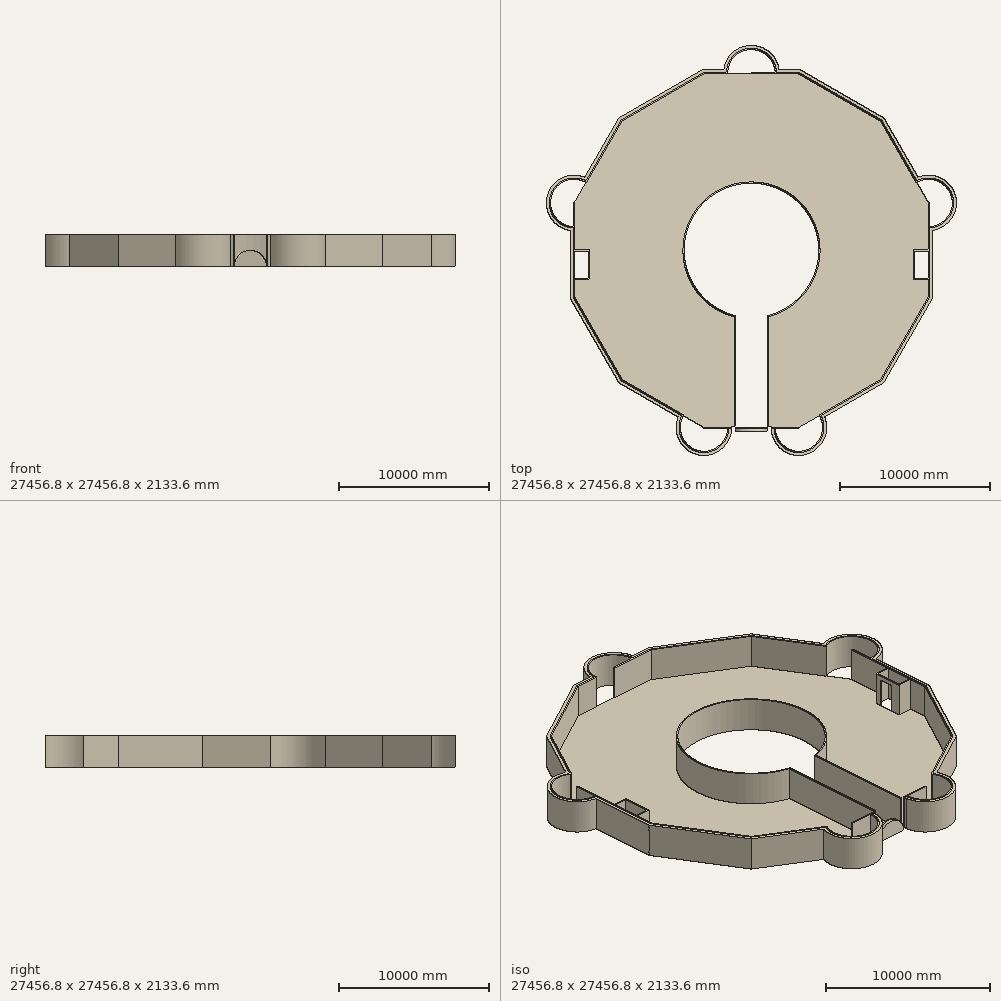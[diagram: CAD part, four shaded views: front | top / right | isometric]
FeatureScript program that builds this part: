
annotation { "Feature Type Name" : "Feature", "Feature Type Description" : "" }
export const myFeature = defineFeature(function(context is Context, id is Id, definition is map)
    precondition{}
    {
        {
            var Q0;
            Q0=qCreatedBy(makeId("Top.planeOp"),FACE);
            var sketch = newSketch(context, id + "F0", { "sketchPlane" : qUnion([Q0])});
            skLineSegment(sketch, "E0.1.15", {"start": v(-8653.47, 8653.47) * mm, "end": v(-3167.4, 11820.87) * mm});
            skLineSegment(sketch, "E0.1.18", {"start": v(-3191.21, 11909.77) * mm, "end": v(-8718.55, 8718.55) * mm});
            skLineSegment(sketch, "E0.2.6", {"start": v(-8653.47, 8653.47) * mm, "end": v(-11034.98, 4528.6) * mm});
            skLineSegment(sketch, "E1", {"start": v(-11909.77, 1507.3) * mm, "end": v(-11909.77, 0) * mm});
            skLineSegment(sketch, "E2", {"start": v(-3191.21, 11909.77) * mm, "end": v(-1672, 11909.77) * mm});
            skLineSegment(sketch, "E3", {"start": v(-3167.4, 11820.87) * mm, "end": v(-1583.7, 11820.87) * mm});
            skLineSegment(sketch, "E4.1.9", {"start": v(-8653.47, -8653.47) * mm, "end": v(-11820.87, -3167.4) * mm});
            skLineSegment(sketch, "E4.1.12", {"start": v(-4528.6, -11034.97) * mm, "end": v(-8653.47, -8653.47) * mm});
            skLineSegment(sketch, "E4.1.27", {"start": v(-1507.3, -11909.77) * mm, "end": v(0, -11909.77) * mm});
            skLineSegment(sketch, "E4.1.36", {"start": v(-8718.55, -8718.55) * mm, "end": v(-11909.77, -3191.21) * mm});
            skLineSegment(sketch, "E4.2.4", {"start": v(3167.4, -11820.87) * mm, "end": v(1156.97, -11820.87) * mm});
            skLineSegment(sketch, "E4.2.22", {"start": v(1507.3, -11909.77) * mm, "end": v(0, -11909.77) * mm});
            skLineSegment(sketch, "E5", {"start": v(-3191.21, -11909.77) * mm, "end": v(-3167.4, -11820.87) * mm});
            skLineSegment(sketch, "E6", {"start": v(0, -11820.87) * mm, "end": v(0, -11909.77) * mm});
            skArc(sketch, "E7.MirrorCS", {"start": v(-1596.23, -11909.77) * mm, "mid": v(-3610.62, -13389.15) * mm, "end": v(-4550.82, -11073.47) * mm});
            skLineSegment(sketch, "E8", {"start": v(-11909.77, 3191.21) * mm, "end": v(-11820.87, 3167.4) * mm});
            skArc(sketch, "E9", {"start": v(-11909.77, 1596.24) * mm, "mid": v(-13389.14, 3610.62) * mm, "end": v(-11073.47, 4550.82) * mm});
            skArc(sketch, "E10", {"start": v(1583.07, 11909.77) * mm, "mid": v(-22.23, 13448.85) * mm, "end": v(-1583.69, 11865.32) * mm});
            skLineSegment(sketch, "E11", {"start": v(0, 11909.77) * mm, "end": v(0, 11820.87) * mm});
            skArc(sketch, "E12.MirrorCS", {"start": v(-4649.52, -11067.81) * mm, "mid": v(-3612.2, -13480.91) * mm, "end": v(-1507.3, -11909.77) * mm});
            skLineSegment(sketch, "E13.trimOffspring", {"start": v(-4649.52, -11067.81) * mm, "end": v(-8718.55, -8718.55) * mm});
            skArc(sketch, "E14", {"start": v(-11909.77, 1507.3) * mm, "mid": v(-13480.91, 3612.2) * mm, "end": v(-11067.81, 4649.52) * mm});
            skLineSegment(sketch, "E15.trimOffspring", {"start": v(-11067.81, 4649.52) * mm, "end": v(-8718.55, 8718.55) * mm});
            skArc(sketch, "E16", {"start": v(1672, 11909.77) * mm, "mid": v(0, 13537.9) * mm, "end": v(-1672, 11909.77) * mm});
            skLineSegment(sketch, "E17.3", {"start": v(1332.74, -12112.97) * mm, "end": v(-1332.74, -12112.97) * mm});
            skLineSegment(sketch, "E17.4", {"start": v(-4902.3, -11156.5) * mm, "end": v(-8867.3, -8867.3) * mm});
            skLineSegment(sketch, "E17.5", {"start": v(-8867.3, -8867.3) * mm, "end": v(-12112.97, -3245.66) * mm});
            skLineSegment(sketch, "E17.6", {"start": v(-12112.97, -3245.66) * mm, "end": v(-12112.97, 1332.74) * mm});
            skLineSegment(sketch, "E17.7", {"start": v(-11156.5, 4902.3) * mm, "end": v(-8867.3, 8867.3) * mm});
            skLineSegment(sketch, "E17.8", {"start": v(-8867.3, 8867.3) * mm, "end": v(-3245.66, 12112.97) * mm});
            skLineSegment(sketch, "E17.9", {"start": v(-3245.66, 12112.97) * mm, "end": v(-1846.56, 12112.97) * mm});
            skArc(sketch, "E18", {"start": v(-12112.97, 1332.74) * mm, "mid": v(-13664.92, 3661.5) * mm, "end": v(-11156.5, 4902.3) * mm});
            skArc(sketch, "E19", {"start": v(1846.56, 12112.97) * mm, "mid": v(0, 13728.4) * mm, "end": v(-1846.56, 12112.97) * mm});
            skArc(sketch, "E20", {"start": v(-4902.3, -11156.5) * mm, "mid": v(-3661.5, -13664.92) * mm, "end": v(-1332.74, -12112.97) * mm});
            skLineSegment(sketch, "E21", {"start": v(-1068.07, -4377.26) * mm, "end": v(-1068.07, -11820.87) * mm});
            skArc(sketch, "E22", {"start": v(1068.07, -4377.27) * mm, "mid": v(0, 4505.67) * mm, "end": v(-1068.07, -4377.26) * mm});
            skLineSegment(sketch, "E23.left", {"start": v(-11909.77, 0) * mm, "end": v(-11909.77, -3191.21) * mm});
            skLineSegment(sketch, "E24", {"start": v(-11820.87, 1595.61) * mm, "end": v(-11820.87, 44.45) * mm});
            skLineSegment(sketch, "E25.top", {"start": v(-11820.87, -44.45) * mm, "end": v(-11820.87, -44.45) * mm});
            skLineSegment(sketch, "E26", {"start": v(-11820.87, -3167.4) * mm, "end": v(-11820.87, -1962.15) * mm});
            skLineSegment(sketch, "E27", {"start": v(-10817.57, 44.45) * mm, "end": v(-10817.57, -1962.15) * mm});
            skLineSegment(sketch, "E28", {"start": v(-10906.47, -44.45) * mm, "end": v(-11820.87, -44.45) * mm});
            skLineSegment(sketch, "E29", {"start": v(-11820.87, 44.45) * mm, "end": v(-10817.57, 44.45) * mm});
            skLineSegment(sketch, "E30.trimOffspring", {"start": v(-11820.87, -1873.25) * mm, "end": v(-11820.87, -44.45) * mm});
            skLineSegment(sketch, "E31", {"start": v(-10906.47, -44.45) * mm, "end": v(-10906.47, -349.25) * mm});
            skLineSegment(sketch, "E32", {"start": v(-10906.47, -349.25) * mm, "end": v(-11820.87, -349.25) * mm});
            skLineSegment(sketch, "E33", {"start": v(-10906.47, -349.25) * mm, "end": v(-10906.47, -1873.25) * mm});
            skLineSegment(sketch, "E34", {"start": v(-10906.47, -349.25) * mm, "end": v(-10817.57, -349.25) * mm});
            skLineSegment(sketch, "E35", {"start": v(-10906.47, -1263.65) * mm, "end": v(-10817.57, -1263.65) * mm});
            skEllipse(sketch, "E36", {"center": v(-11321.44, -1568.45) * mm, "majorRadius": 254 * mm, "minorRadius": 304.8 * mm, "majorAxis": v(-1, 0)});
            skLineSegment(sketch, "E37", {"start": v(-11820.87, -1873.25) * mm, "end": v(-10906.47, -1873.25) * mm});
            skLineSegment(sketch, "E38", {"start": v(-11820.87, -1962.15) * mm, "end": v(-10817.57, -1962.15) * mm});
            skLineSegment(sketch, "E39", {"start": v(-3167.4, -11820.87) * mm, "end": v(-1156.97, -11820.87) * mm});
            skLineSegment(sketch, "E40", {"start": v(-3191.21, -11909.77) * mm, "end": v(-1596.23, -11909.77) * mm});
            skLineSegment(sketch, "E41", {"start": v(-4550.82, -11073.47) * mm, "end": v(-4528.6, -11034.97) * mm});
            skLineSegment(sketch, "E42", {"start": v(-11909.77, 3191.21) * mm, "end": v(-11909.77, 1596.24) * mm});
            skLineSegment(sketch, "E43", {"start": v(-11820.87, 3167.4) * mm, "end": v(-11820.87, 1595.61) * mm});
            skLineSegment(sketch, "E44", {"start": v(-11073.47, 4550.82) * mm, "end": v(-11034.98, 4528.6) * mm});
            skLineSegment(sketch, "E45", {"start": v(0, 11909.77) * mm, "end": v(1583.07, 11909.77) * mm});
            skLineSegment(sketch, "E46", {"start": v(0, 11820.87) * mm, "end": v(1583.7, 11820.87) * mm});
            skLineSegment(sketch, "E47", {"start": v(-1583.7, 11865.32) * mm, "end": v(-1583.7, 11820.87) * mm});
            skArc(sketch, "E48.MirrorCS", {"start": v(12112.97, 1332.74) * mm, "mid": v(13664.92, 3661.5) * mm, "end": v(11156.5, 4902.3) * mm});
            skLineSegment(sketch, "E49.MirrorCS", {"start": v(11820.87, 3167.4) * mm, "end": v(11820.87, 1595.61) * mm});
            skLineSegment(sketch, "E50.MirrorCS", {"start": v(11909.77, 1507.3) * mm, "end": v(11909.77, 0) * mm});
            skLineSegment(sketch, "E51.MirrorCS", {"start": v(11909.77, 3191.21) * mm, "end": v(11909.77, 1596.24) * mm});
            skLineSegment(sketch, "E52.MirrorCS", {"start": v(3191.21, -11909.77) * mm, "end": v(3167.4, -11820.87) * mm});
            skLineSegment(sketch, "E53.MirrorCS", {"start": v(11909.77, 3191.21) * mm, "end": v(11820.87, 3167.4) * mm});
            skLineSegment(sketch, "E54.MirrorCS", {"start": v(11820.87, 1595.61) * mm, "end": v(11820.87, 44.45) * mm});
            skLineSegment(sketch, "E55.MirrorCS", {"start": v(10906.47, -44.45) * mm, "end": v(11820.87, -44.45) * mm});
            skLineSegment(sketch, "E56.MirrorCS", {"start": v(10906.47, -349.25) * mm, "end": v(11820.87, -349.25) * mm});
            skLineSegment(sketch, "E57.MirrorCS", {"start": v(11820.87, 44.45) * mm, "end": v(10817.57, 44.45) * mm});
            skLineSegment(sketch, "E58.MirrorCS", {"start": v(10906.47, -44.45) * mm, "end": v(10906.47, -349.25) * mm});
            skLineSegment(sketch, "E59.MirrorCS", {"start": v(10906.47, -349.25) * mm, "end": v(10817.57, -349.25) * mm});
            skLineSegment(sketch, "E60.MirrorCS", {"start": v(10817.57, 44.45) * mm, "end": v(10817.57, -1962.15) * mm});
            skLineSegment(sketch, "E61.MirrorCS", {"start": v(1583.69, 11865.32) * mm, "end": v(1583.69, 11820.87) * mm});
            skLineSegment(sketch, "E62.MirrorCS", {"start": v(3191.21, 11909.77) * mm, "end": v(1672, 11909.77) * mm});
            skLineSegment(sketch, "E63.MirrorCS", {"start": v(11820.87, -1873.25) * mm, "end": v(11820.87, -44.45) * mm});
            skLineSegment(sketch, "E64.MirrorCS", {"start": v(11820.87, -1873.25) * mm, "end": v(10906.47, -1873.25) * mm});
            skLineSegment(sketch, "E65.MirrorCS", {"start": v(10906.47, -349.25) * mm, "end": v(10906.47, -1873.25) * mm});
            skLineSegment(sketch, "E66.MirrorCS", {"start": v(11820.87, -3167.4) * mm, "end": v(11820.87, -1962.15) * mm});
            skLineSegment(sketch, "E67.MirrorCS", {"start": v(10906.47, -1263.65) * mm, "end": v(10817.57, -1263.65) * mm});
            skLineSegment(sketch, "E68.MirrorCS", {"start": v(12112.97, -3245.66) * mm, "end": v(12112.97, 1332.74) * mm});
            skLineSegment(sketch, "E69.MirrorCS", {"start": v(3167.4, 11820.87) * mm, "end": v(1583.69, 11820.87) * mm});
            skLineSegment(sketch, "E70.MirrorCS", {"start": v(11820.87, -1962.15) * mm, "end": v(10817.57, -1962.15) * mm});
            skEllipse(sketch, "E71.MirrorC", {"center": v(11321.44, -1568.45) * mm, "majorRadius": 254 * mm, "minorRadius": 304.8 * mm, "majorAxis": v(1, 0)});
            skLineSegment(sketch, "E72.MirrorCS", {"start": v(3191.21, -11909.77) * mm, "end": v(1596.23, -11909.77) * mm});
            skLineSegment(sketch, "E73.MirrorCS", {"start": v(11909.77, 0) * mm, "end": v(11909.77, -3191.21) * mm});
            skLineSegment(sketch, "E74.MirrorCS", {"start": v(3245.66, 12112.97) * mm, "end": v(1846.56, 12112.97) * mm});
            skLineSegment(sketch, "E75.MirrorCS", {"start": v(4550.82, -11073.47) * mm, "end": v(4528.6, -11034.97) * mm});
            skLineSegment(sketch, "E76.MirrorCS", {"start": v(11073.47, 4550.82) * mm, "end": v(11034.98, 4528.6) * mm});
            skArc(sketch, "E77.MirrorCS", {"start": v(4649.52, -11067.81) * mm, "mid": v(3612.2, -13480.91) * mm, "end": v(1507.3, -11909.77) * mm});
            skLineSegment(sketch, "E78.MirrorCS", {"start": v(8653.47, 8653.47) * mm, "end": v(3167.4, 11820.87) * mm});
            skLineSegment(sketch, "E79.MirrorCS", {"start": v(8867.3, 8867.3) * mm, "end": v(3245.66, 12112.97) * mm});
            skLineSegment(sketch, "E80.MirrorCS", {"start": v(4649.52, -11067.81) * mm, "end": v(8718.55, -8718.55) * mm});
            skLineSegment(sketch, "E81.MirrorCS", {"start": v(11067.81, 4649.52) * mm, "end": v(8718.55, 8718.55) * mm});
            skLineSegment(sketch, "E82.MirrorCS", {"start": v(4902.3, -11156.5) * mm, "end": v(8867.3, -8867.3) * mm});
            skLineSegment(sketch, "E83.MirrorCS", {"start": v(8718.55, -8718.55) * mm, "end": v(11909.77, -3191.21) * mm});
            skLineSegment(sketch, "E84.MirrorCS", {"start": v(4528.6, -11034.97) * mm, "end": v(8653.47, -8653.47) * mm});
            skLineSegment(sketch, "E85.MirrorCS", {"start": v(8653.47, -8653.47) * mm, "end": v(11820.87, -3167.4) * mm});
            skLineSegment(sketch, "E86.MirrorCS", {"start": v(11156.5, 4902.3) * mm, "end": v(8867.3, 8867.3) * mm});
            skLineSegment(sketch, "E87.MirrorCS", {"start": v(8653.47, 8653.47) * mm, "end": v(11034.98, 4528.6) * mm});
            skLineSegment(sketch, "E88.MirrorCS", {"start": v(8867.3, -8867.3) * mm, "end": v(12112.97, -3245.66) * mm});
            skArc(sketch, "E89.MirrorCS", {"start": v(4902.3, -11156.5) * mm, "mid": v(3661.5, -13664.92) * mm, "end": v(1332.74, -12112.97) * mm});
            skLineSegment(sketch, "E90.MirrorCS", {"start": v(1068.07, -4377.26) * mm, "end": v(1068.07, -11820.87) * mm});
            skLineSegment(sketch, "E91.MirrorCS", {"start": v(3191.21, 11909.77) * mm, "end": v(8718.55, 8718.55) * mm});
            skArc(sketch, "E92.MirrorCS", {"start": v(11909.77, 1596.24) * mm, "mid": v(13389.14, 3610.62) * mm, "end": v(11073.47, 4550.82) * mm});
            skArc(sketch, "E93.MirrorCS", {"start": v(11909.77, 1507.3) * mm, "mid": v(13480.91, 3612.2) * mm, "end": v(11067.81, 4649.52) * mm});
            skArc(sketch, "E94.MirrorCS", {"start": v(1596.23, -11909.77) * mm, "mid": v(3610.62, -13389.15) * mm, "end": v(4550.82, -11073.47) * mm});
            skLineSegment(sketch, "E95", {"start": v(-1156.97, -11820.87) * mm, "end": v(-1156.97, -4446.52) * mm});
            skLineSegment(sketch, "E96.MirrorCS", {"start": v(1156.97, -11820.87) * mm, "end": v(1156.97, -4446.52) * mm});
            skLineSegment(sketch, "E97.trimOffspring", {"start": v(1068.07, -11820.87) * mm, "end": v(0, -11820.87) * mm});
            skLineSegment(sketch, "E98.trimOffspring", {"start": v(-1068.07, -11820.87) * mm, "end": v(0, -11820.87) * mm});
            skArc(sketch, "E99.trimOffspring", {"start": v(1156.97, -4446.52) * mm, "mid": v(0, 4594.58) * mm, "end": v(-1156.97, -4446.52) * mm});
            skLineSegment(sketch, "E100.top", {"start": v(-10906.47, -1873.25) * mm, "end": v(-11820.87, -1873.25) * mm});
            skLineSegment(sketch, "E100.right", {"start": v(-11820.87, -349.25) * mm, "end": v(-11820.87, -1873.25) * mm});
            skLineSegment(sketch, "E101.bottom", {"start": v(-10817.57, -349.25) * mm, "end": v(-10906.47, -349.25) * mm});
            skLineSegment(sketch, "E101.top", {"start": v(-10817.57, -1263.65) * mm, "end": v(-10906.47, -1263.65) * mm});
            skLineSegment(sketch, "E101.left", {"start": v(-10817.57, -349.25) * mm, "end": v(-10817.57, -1263.65) * mm});
            skLineSegment(sketch, "E101.right", {"start": v(-10906.47, -349.25) * mm, "end": v(-10906.47, -1263.65) * mm});
            skLineSegment(sketch, "E102.bottom", {"start": v(11820.87, -349.25) * mm, "end": v(10906.47, -349.25) * mm});
            skLineSegment(sketch, "E102.left", {"start": v(11820.87, -349.25) * mm, "end": v(11820.87, -1873.25) * mm});
            skLineSegment(sketch, "E103.left", {"start": v(10906.47, -349.25) * mm, "end": v(10906.47, -1263.65) * mm});
            skLineSegment(sketch, "E103.right", {"start": v(10817.57, -349.25) * mm, "end": v(10817.57, -1263.65) * mm});
            skLineSegment(sketch, "E104", {"start": v(-11865.32, 3179.3) * mm, "end": v(-11073.47, 4550.82) * mm});
            skLineSegment(sketch, "E105", {"start": v(11865.32, 3179.3) * mm, "end": v(11073.47, 4550.82) * mm});
            skLineSegment(sketch, "E106", {"start": v(3179.3, -11865.32) * mm, "end": v(4550.82, -11073.47) * mm});
            skLineSegment(sketch, "E107", {"start": v(-4550.82, -11073.47) * mm, "end": v(-3179.3, -11865.32) * mm});
            skLineSegment(sketch, "E108", {"start": v(-1583.7, 11865.32) * mm, "end": v(0, 11865.32) * mm});
            skSolve(sketch);
        }
        {
            var Q0;
            Q0=makeQuery(id+"F0.imprint","IMPRINT",FACE,{"disambiguationData":[TD([[makeQuery(id+"F0.imprint","IMPRINT",EDGE,{"derivedFrom":sQuery(id+"F0.wireOp",EDGE,"E0.1.15")}),1.0]])]});
            var Q1;
            {var subQ0=sQuery(id+"F0.wireOp",EDGE,"E34");Q1=makeQuery(id+"F0.imprint","IMPRINT",FACE,{"disambiguationData":[TD([[makeQuery(id+"F0.imprint","IMPRINT",EDGE,{"derivedFrom":subQ0}),-1.0]])]});}
            var Q2;
            {var subQ0=sQuery(id+"F0.wireOp",EDGE,"E59.MirrorCS");Q2=makeQuery(id+"F0.imprint","IMPRINT",FACE,{"disambiguationData":[TD([[makeQuery(id+"F0.imprint","IMPRINT",EDGE,{"derivedFrom":subQ0}),1.0]])]});}
            var Q3;
            Q3=makeQuery(id+"F0.imprint","IMPRINT",FACE,{"disambiguationData":[TD([[makeQuery(id+"F0.imprint","IMPRINT",EDGE,{"derivedFrom":sQuery(id+"F0.wireOp",EDGE,"E101.bottom")}),1.0]])]});
            var Q4;
            Q4=makeQuery(id+"F0.imprint","IMPRINT",FACE,{"disambiguationData":[TD([[makeQuery(id+"F0.imprint","IMPRINT",EDGE,{"derivedFrom":sQuery(id+"F0.wireOp",EDGE,"E59.MirrorCS")}),1.0]])]});
            extrude(context, id + "F1", {"entities" : qUnion([Q0, Q1, Q2, Q3, Q4]), "depth" : 2133.6 * mm});
        }
        {
            var Q0;
            Q0=makeQuery(id+"F0.imprint","IMPRINT",FACE,{"disambiguationData":[TD([[makeQuery(id+"F0.imprint","IMPRINT",EDGE,{"derivedFrom":sQuery(id+"F0.wireOp",EDGE,"E0.1.18")}),-1.0]])]});
            extrude(context, id + "F2", {"entities" : qUnion([Q0]), "depth" : 2133.6 * mm});
        }
        {
            var Q0;
            Q0=makeQuery(id+"F0.imprint","IMPRINT",FACE,{"disambiguationData":[TD([[makeQuery(id+"F0.imprint","IMPRINT",EDGE,{"derivedFrom":sQuery(id+"F0.wireOp",EDGE,"E0.1.15")}),-1.0]])]});
            extrude(context, id + "F3", {"entities" : qUnion([Q0]), "operationType" : NewBodyOperationType.ADD, "depth" : 25.4 * mm});
        }
        {
            var Q0;
            Q0=makeQuery(id+"F0.imprint","IMPRINT",FACE,{"disambiguationData":[TD([[makeQuery(id+"F0.imprint","IMPRINT",EDGE,{"derivedFrom":sQuery(id+"F0.wireOp",EDGE,"E101.bottom")}),1.0]])]});
            var Q1;
            Q1=makeQuery(id+"F0.imprint","IMPRINT",FACE,{"disambiguationData":[TD([[makeQuery(id+"F0.imprint","IMPRINT",EDGE,{"derivedFrom":sQuery(id+"F0.wireOp",EDGE,"E59.MirrorCS")}),1.0]])]});
            extrude(context, id + "F4", {"entities" : qUnion([Q0, Q1]), "operationType" : NewBodyOperationType.REMOVE, "depth" : 1828.8 * mm});
        }
        {
            var Q0;
            Q0=makeQuery(id+"F2.opExtrude","SWEPT_FACE",FACE,{"disambiguationData":[OSD([sQuery(id+"F0.wireOp",EDGE,"E17.3")])]});
            var sketch = newSketch(context, id + "F5", { "sketchPlane" : qUnion([Q0])});
            skArc(sketch, "E109", {"start": v(-1066.8, 0) * mm, "mid": v(0, 1066.8) * mm, "end": v(1066.8, 0) * mm});
            skSolve(sketch);
        }
        {
            var Q0;
            {var subQ0=sQuery(id+"F5.wireOp",EDGE,"E109");Q0=makeQuery(id+"F5.imprint","IMPRINT",FACE,{"disambiguationData":[TD([[makeQuery(id+"F5.imprint","IMPRINT",EDGE,{"derivedFrom":subQ0}),-1.0]])]});}
            extrude(context, id + "F6", {"entities" : qUnion([Q0]), "operationType" : NewBodyOperationType.REMOVE, "oppositeDirection" : true, "depth" : 304.8 * mm});
        }
    });
